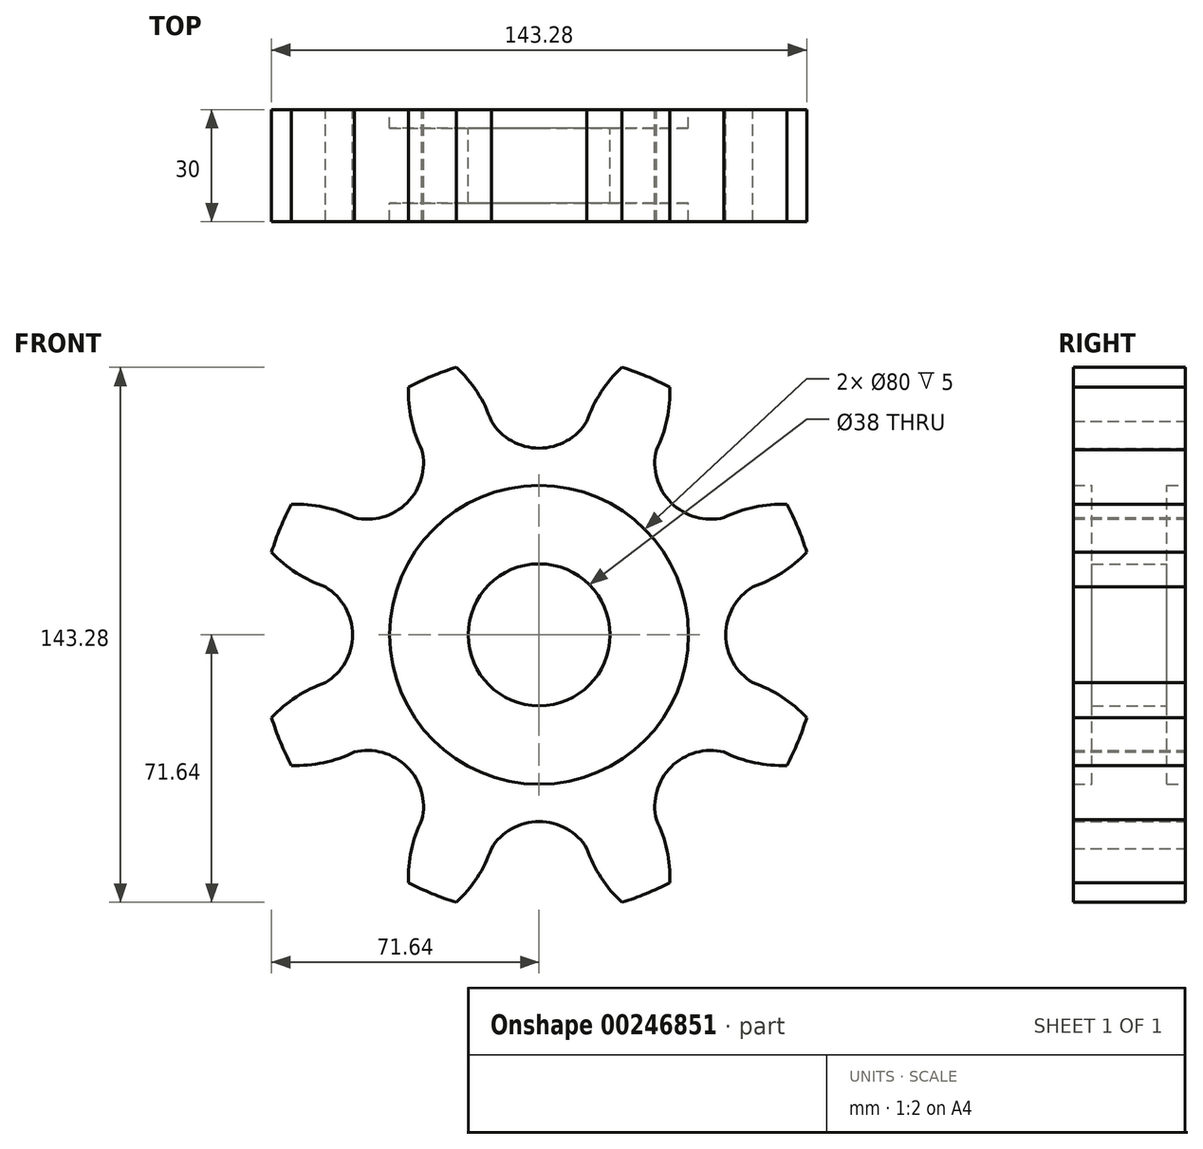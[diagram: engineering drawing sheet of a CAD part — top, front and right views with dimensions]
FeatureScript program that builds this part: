
annotation { "Feature Type Name" : "Feature", "Feature Type Description" : "" }
export const myFeature = defineFeature(function(context is Context, id is Id, definition is map)
    precondition{}
    {
        {
            var Q0;
            Q0=qCreatedBy(makeId("Front.planeOp"),FACE);
            var sketch = newSketch(context, id + "F0", { "sketchPlane" : qUnion([Q0])});
            skCircle(sketch, "E0", {"center": v(0, 0) * mm, "radius": 19 * mm});
            skCircle(sketch, "E1", {"center": v(0, 0) * mm, "radius": 65 * mm, "construction": true});
            skCircle(sketch, "E2", {"center": v(0, 0) * mm, "radius": 40 * mm});
            skArc(sketch, "E3", {"start": v(34.97, 66.35) * mm, "mid": v(28.7, 69.3) * mm, "end": v(22.18, 71.64) * mm});
            skArc(sketch, "E4", {"start": v(-34.97, 66.35) * mm, "mid": v(-34.23, 57.7) * mm, "end": v(-31.39, 49.52) * mm});
            skArc(sketch, "E5.1.0", {"start": v(-49.52, 31.39) * mm, "mid": v(-35.36, 35.36) * mm, "end": v(-31.39, 49.52) * mm});
            skArc(sketch, "E5.2.0", {"start": v(-57.21, -12.82) * mm, "mid": v(-50, 0) * mm, "end": v(-57.21, 12.82) * mm});
            skArc(sketch, "E6.1.0", {"start": v(-71.64, 22.18) * mm, "mid": v(-65.01, 16.6) * mm, "end": v(-57.21, 12.82) * mm});
            skArc(sketch, "E6.2.0", {"start": v(-66.35, -34.97) * mm, "mid": v(-57.7, -34.23) * mm, "end": v(-49.52, -31.39) * mm});
            skArc(sketch, "E6.3.0", {"start": v(-57.21, -12.82) * mm, "mid": v(-65.01, -16.6) * mm, "end": v(-71.64, -22.18) * mm});
            skArc(sketch, "E6.4.0", {"start": v(-31.39, -49.52) * mm, "mid": v(-34.23, -57.7) * mm, "end": v(-34.97, -66.35) * mm});
            skArc(sketch, "E6.5.0", {"start": v(12.82, -57.21) * mm, "mid": v(16.6, -65.01) * mm, "end": v(22.18, -71.64) * mm});
            skArc(sketch, "E6.6.0", {"start": v(66.35, 34.97) * mm, "mid": v(57.7, 34.23) * mm, "end": v(49.52, 31.39) * mm});
            skArc(sketch, "E6.7.0", {"start": v(22.18, 71.64) * mm, "mid": v(16.6, 65.01) * mm, "end": v(12.82, 57.21) * mm});
            skArc(sketch, "E7.trimOffspring", {"start": v(57.21, 12.82) * mm, "mid": v(65.01, 16.6) * mm, "end": v(71.64, 22.18) * mm});
            skArc(sketch, "E8.trimOffspring", {"start": v(31.39, 49.52) * mm, "mid": v(34.23, 57.7) * mm, "end": v(34.97, 66.35) * mm});
            skArc(sketch, "E9.trimOffspring", {"start": v(-22.18, 71.64) * mm, "mid": v(-28.7, 69.3) * mm, "end": v(-34.97, 66.35) * mm});
            skArc(sketch, "E10.trimOffspring", {"start": v(-66.35, 34.97) * mm, "mid": v(-69.3, 28.7) * mm, "end": v(-71.64, 22.18) * mm});
            skArc(sketch, "E11.trimOffspring", {"start": v(-49.52, 31.39) * mm, "mid": v(-57.7, 34.23) * mm, "end": v(-66.35, 34.97) * mm});
            skArc(sketch, "E12.trimOffspring", {"start": v(-12.82, 57.21) * mm, "mid": v(-16.6, 65.01) * mm, "end": v(-22.18, 71.64) * mm});
            skArc(sketch, "E13.trimOffspring", {"start": v(-71.64, -22.18) * mm, "mid": v(-69.3, -28.7) * mm, "end": v(-66.35, -34.97) * mm});
            skArc(sketch, "E14.trimOffspring", {"start": v(-22.18, -71.64) * mm, "mid": v(-16.6, -65.01) * mm, "end": v(-12.82, -57.21) * mm});
            skArc(sketch, "E15.trimOffspring", {"start": v(-34.97, -66.35) * mm, "mid": v(-28.7, -69.3) * mm, "end": v(-22.18, -71.64) * mm});
            skArc(sketch, "E16.trimOffspring", {"start": v(22.18, -71.64) * mm, "mid": v(28.7, -69.3) * mm, "end": v(34.97, -66.35) * mm});
            skArc(sketch, "E17.trimOffspring", {"start": v(34.97, -66.35) * mm, "mid": v(34.23, -57.7) * mm, "end": v(31.39, -49.52) * mm});
            skArc(sketch, "E18.trimOffspring", {"start": v(71.64, 22.18) * mm, "mid": v(69.3, 28.7) * mm, "end": v(66.35, 34.97) * mm});
            skArc(sketch, "E19.trimOffspring", {"start": v(71.64, -22.18) * mm, "mid": v(65.01, -16.6) * mm, "end": v(57.21, -12.82) * mm});
            skArc(sketch, "E20.trimOffspring", {"start": v(66.35, -34.97) * mm, "mid": v(69.3, -28.7) * mm, "end": v(71.64, -22.18) * mm});
            skArc(sketch, "E21.trimOffspring", {"start": v(12.82, -57.21) * mm, "mid": v(0, -50) * mm, "end": v(-12.82, -57.21) * mm});
            skArc(sketch, "E22.trimOffspring", {"start": v(49.52, -31.39) * mm, "mid": v(35.36, -35.36) * mm, "end": v(31.39, -49.52) * mm});
            skArc(sketch, "E23.trimOffspring", {"start": v(49.52, -31.39) * mm, "mid": v(57.7, -34.23) * mm, "end": v(66.35, -34.97) * mm});
            skArc(sketch, "E24.trimOffspring", {"start": v(57.21, 12.82) * mm, "mid": v(50, 0) * mm, "end": v(57.21, -12.82) * mm});
            skArc(sketch, "E25.trimOffspring", {"start": v(-31.39, -49.52) * mm, "mid": v(-35.36, -35.36) * mm, "end": v(-49.52, -31.39) * mm});
            skArc(sketch, "E26.trimOffspring", {"start": v(31.39, 49.52) * mm, "mid": v(35.36, 35.36) * mm, "end": v(49.52, 31.39) * mm});
            skArc(sketch, "E27.trimOffspring", {"start": v(-12.82, 57.21) * mm, "mid": v(0, 50) * mm, "end": v(12.82, 57.21) * mm});
            skSolve(sketch);
        }
        {
            var Q0;
            Q0 = qSketchRegion(id + "F0", true);
            extrude(context, id + "F1", {"entities" : qUnion([Q0]), "depth" : 15 * mm, "hasSecondDirection" : true, "secondDirectionOppositeDirection" : true, "secondDirectionDepth" : 15 * mm});
        }
        {
            var Q0;
            Q0=qCreatedBy(makeId("Front.planeOp"),FACE);
            var sketch = newSketch(context, id + "F2", { "sketchPlane" : qUnion([Q0])});
            skCircle(sketch, "E28", {"center": v(0, 0) * mm, "radius": 19 * mm});
            skCircle(sketch, "E29", {"center": v(0, 0) * mm, "radius": 40 * mm});
            skSolve(sketch);
        }
        {
            var Q0;
            Q0 = qSketchRegion(id + "F2", true);
            extrude(context, id + "F3", {"entities" : qUnion([Q0]), "operationType" : NewBodyOperationType.ADD, "depth" : 10 * mm, "hasSecondDirection" : true, "secondDirectionOppositeDirection" : true, "secondDirectionDepth" : 10 * mm});
        }
    });
